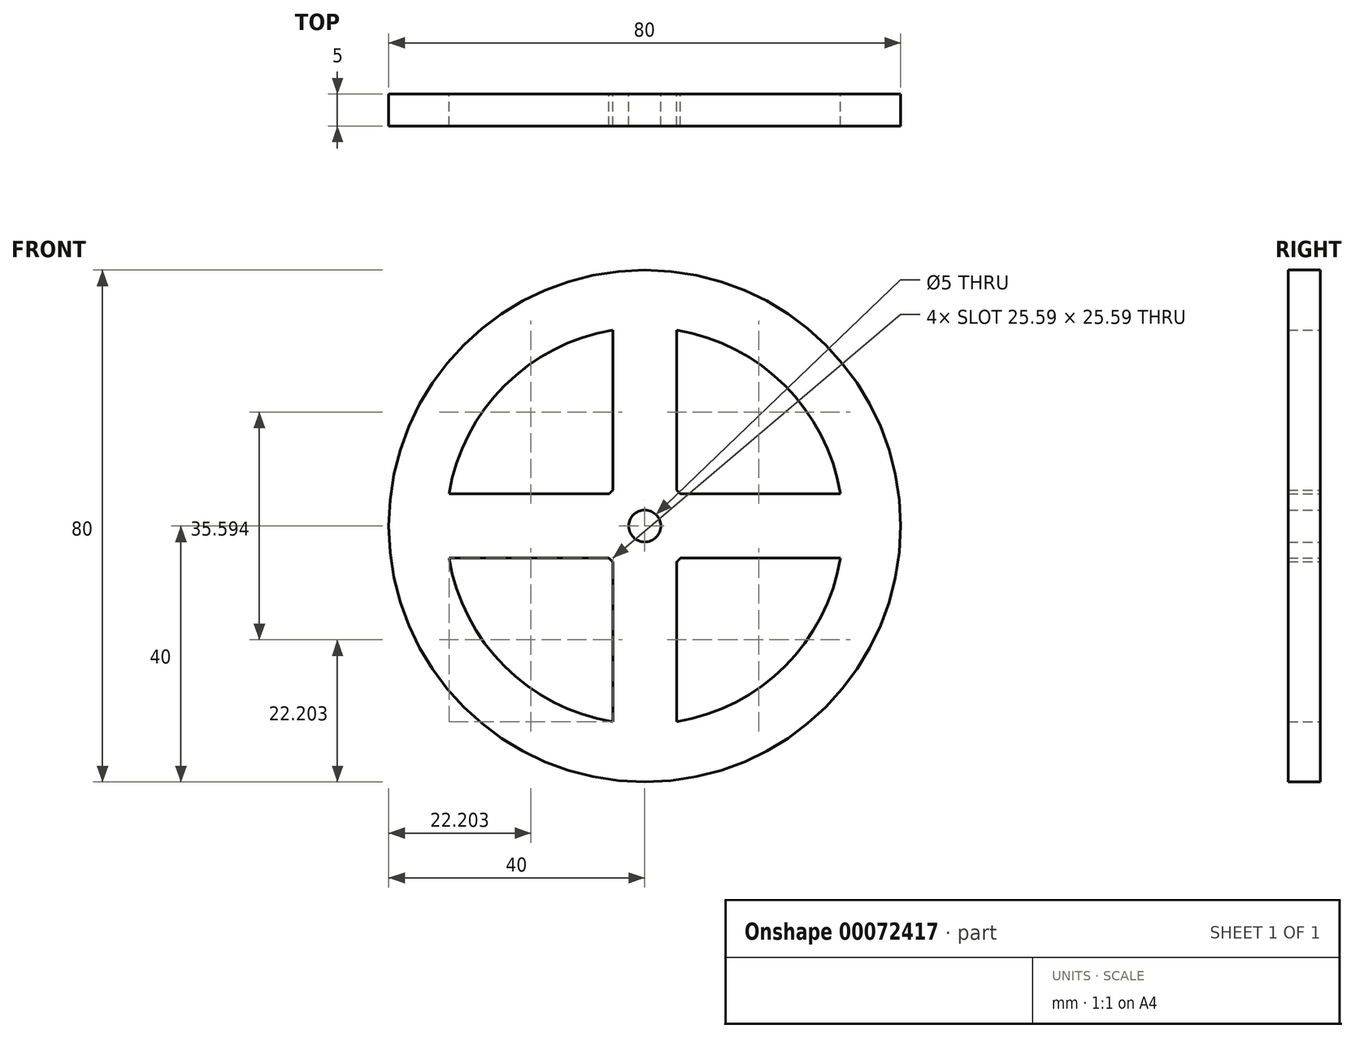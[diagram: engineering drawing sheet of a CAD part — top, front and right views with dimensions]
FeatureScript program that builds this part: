
annotation { "Feature Type Name" : "Feature", "Feature Type Description" : "" }
export const myFeature = defineFeature(function(context is Context, id is Id, definition is map)
    precondition{}
    {
        {
            var Q0;
            Q0=qCreatedBy(makeId("Front.planeOp"),FACE);
            var sketch = newSketch(context, id + "F0", { "sketchPlane" : qUnion([Q0])});
            skArc(sketch, "E0", {"start": v(5, -5.6) * mm, "mid": v(5.3, -5.3) * mm, "end": v(5.6, -5) * mm});
            skCircle(sketch, "E1", {"center": v(0, 0) * mm, "radius": 40 * mm});
            skArc(sketch, "E2", {"start": v(-30.6, -5) * mm, "mid": v(-21.92, -21.92) * mm, "end": v(-5, -30.6) * mm});
            skCircle(sketch, "E3", {"center": v(0, 0) * mm, "radius": 2.5 * mm});
            skLineSegment(sketch, "E4", {"start": v(0, 0) * mm, "end": v(0, 40) * mm, "construction": true});
            skLineSegment(sketch, "E5.0", {"start": v(-5, 5.6) * mm, "end": v(-5, 30.6) * mm});
            skLineSegment(sketch, "E6.0", {"start": v(5, 5.6) * mm, "end": v(5, 30.6) * mm});
            skLineSegment(sketch, "E7", {"start": v(0, 0) * mm, "end": v(-40, 0) * mm, "construction": true});
            skLineSegment(sketch, "E8", {"start": v(0, 0) * mm, "end": v(0, -40) * mm, "construction": true});
            skLineSegment(sketch, "E9", {"start": v(0, 0) * mm, "end": v(2.5, 0) * mm, "construction": true});
            skLineSegment(sketch, "E10.0", {"start": v(-5.6, 5) * mm, "end": v(-30.6, 5) * mm});
            skLineSegment(sketch, "E11.0", {"start": v(-5.6, -5) * mm, "end": v(-30.6, -5) * mm});
            skLineSegment(sketch, "E12.0", {"start": v(-5, -5.6) * mm, "end": v(-5, -30.6) * mm});
            skLineSegment(sketch, "E13.0", {"start": v(5, -5.6) * mm, "end": v(5, -30.6) * mm});
            skLineSegment(sketch, "E14.0", {"start": v(5.6, -5) * mm, "end": v(30.6, -5) * mm});
            skArc(sketch, "E15.trimOffspring", {"start": v(-5, 30.6) * mm, "mid": v(-21.92, 21.92) * mm, "end": v(-30.6, 5) * mm});
            skArc(sketch, "E16.trimOffspring", {"start": v(30.6, 5) * mm, "mid": v(21.92, 21.92) * mm, "end": v(5, 30.6) * mm});
            skArc(sketch, "E17.trimOffspring", {"start": v(5, -30.6) * mm, "mid": v(21.92, -21.92) * mm, "end": v(30.6, -5) * mm});
            skArc(sketch, "E18.trimOffspring", {"start": v(5.6, 5) * mm, "mid": v(5.3, 5.3) * mm, "end": v(5, 5.6) * mm});
            skArc(sketch, "E19.trimOffspring", {"start": v(-5.6, -5) * mm, "mid": v(-5.3, -5.3) * mm, "end": v(-5, -5.6) * mm});
            skArc(sketch, "E20.trimOffspring", {"start": v(-5, 5.6) * mm, "mid": v(-5.3, 5.3) * mm, "end": v(-5.6, 5) * mm});
            skLineSegment(sketch, "E21.trimOffspring", {"start": v(5.6, 5) * mm, "end": v(30.6, 5) * mm});
            skSolve(sketch);
        }
        {
            var Q0;
            Q0=makeQuery(id+"F0.imprint","IMPRINT",FACE,{"disambiguationData":[TD([[makeQuery(id+"F0.imprint","IMPRINT",EDGE,{"derivedFrom":sQuery(id+"F0.wireOp",EDGE,"E0")}),1.0]])]});
            extrude(context, id + "F1", {"entities" : qUnion([Q0]), "endBound" : BoundingType.SYMMETRIC, "depth" : 5 * mm});
        }
    });
